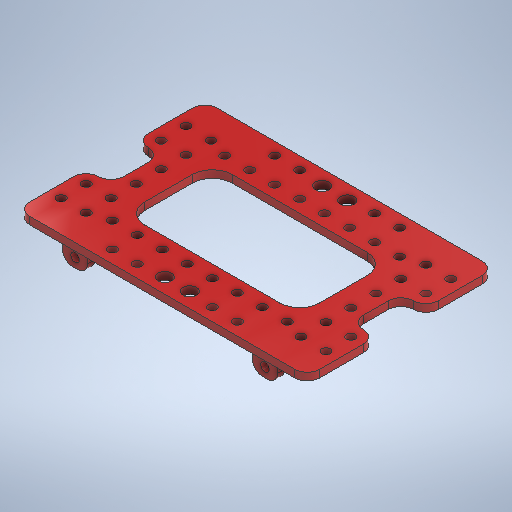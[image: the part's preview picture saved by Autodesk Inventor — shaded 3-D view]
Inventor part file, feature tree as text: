
AUTODESK INVENTOR PART (.ipt)
format: ipt  version: 2025 (Build 290162000, 162)  size: 847,872 bytes
history: native  units: mm
features: fillet x5, extrude x3, sketch x3
ambient origin geometry x8: Origin, YZ Plane, XZ Plane, XY Plane, X Axis, Y Axis, Z Axis, Center Point
bodies: Solide1 (feature_tree)
feature tree (11):
  extrude  "Extrusion1"  Depth=116.0mm
  fillet  "Congé1"  Radius=75.0mm
  fillet  "Congé2"  Radius=3.5mm
  extrude  "Extrusion2"  Depth=3.5mm
  extrude  "Extrusion3"  Depth=10.0mm
  fillet  "Congé3"  Radius=3.5mm
  fillet  "Congé4"  Radius=3.5mm
  fillet  "Congé5"  Radius=3.5mm
  sketch  "Esquisse1"
  sketch  "Esquisse2"
  sketch  "Esquisse3"
